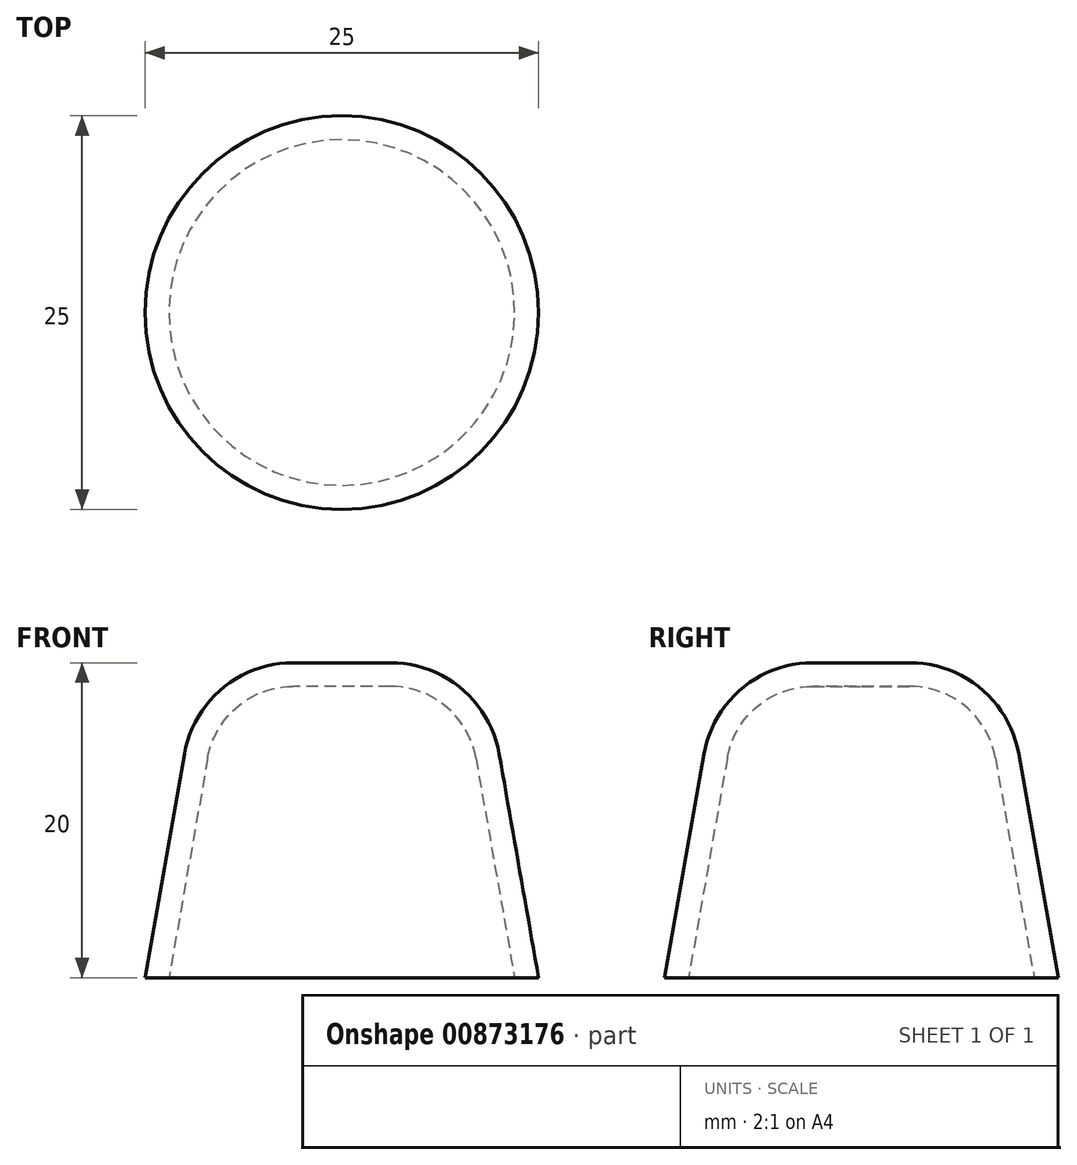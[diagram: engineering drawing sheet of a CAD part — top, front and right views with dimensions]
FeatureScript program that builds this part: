
annotation { "Feature Type Name" : "Feature", "Feature Type Description" : "" }
export const myFeature = defineFeature(function(context is Context, id is Id, definition is map)
    precondition{}
    {
        {
            var Q0;
            Q0=qCreatedBy(makeId("Top.planeOp"),FACE);
            var sketch = newSketch(context, id + "F0", { "sketchPlane" : qUnion([Q0])});
            skCircle(sketch, "E0", {"center": v(0, 0) * mm, "radius": 12.5 * mm});
            skSolve(sketch);
        }
        {
            var Q0;
            Q0=qSketchRegion(id+"F0",true);
            extrude(context, id + "F1", {"entities" : qUnion([Q0]), "depth" : 20 * mm, "offsetDistance" : 25 * mm, "hasDraft" : true, "draftAngle" : 10 * degree, "draftPullDirection" : true});
        }
        {
            var Q0;
            Q0=makeQuery(id+"F1.opExtrude","CAP_FACE",FACE,{"disambiguationData":[OSD([sQuery(id+"F0.wireOp",EDGE,"E0")])],"isStart":false});
            fillet(context, id + "F2", {"entities" : qUnion([Q0]), "radius" : 7 * mm, "tangentPropagation" : true, "allowEdgeOverflow" : false});
        }
        {
            var Q0;
            Q0=makeQuery(id+"F1.opExtrude","CAP_FACE",FACE,{"disambiguationData":[OSD([sQuery(id+"F0.wireOp",EDGE,"E0")])],"isStart":true});
            shell(context, id + "F3", {"entities" : qUnion([Q0]), "thickness" : 1.5 * mm});
        }
    });
